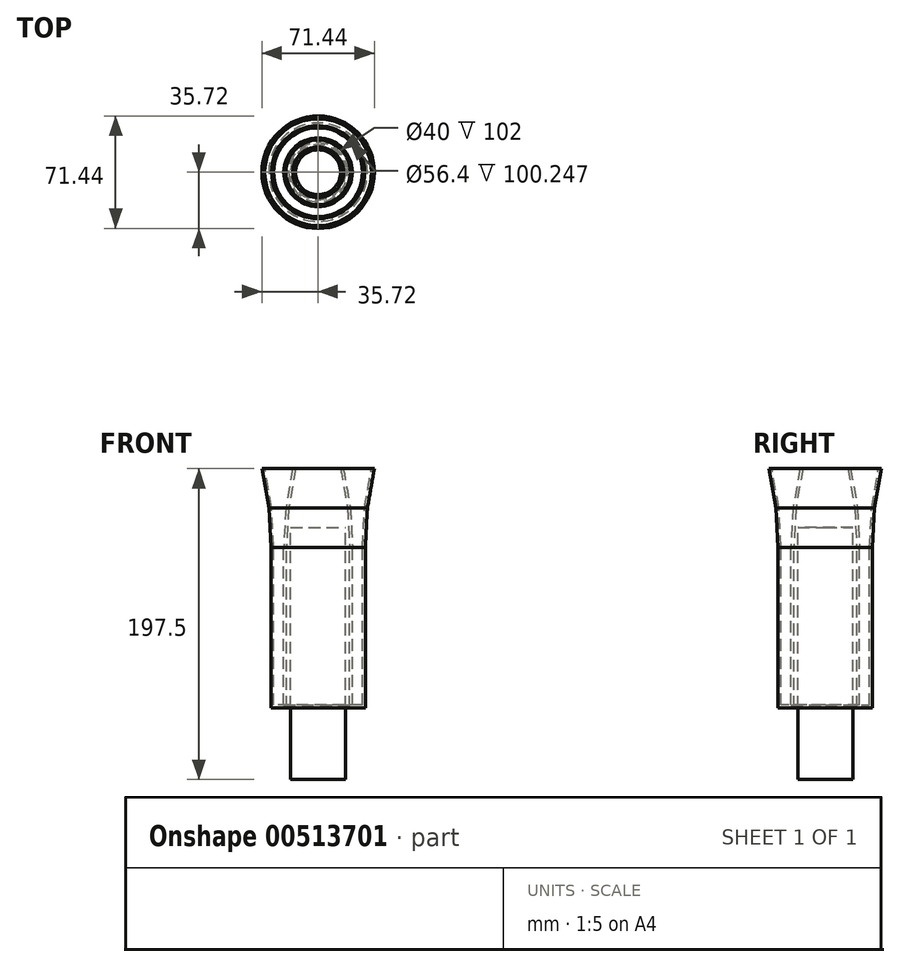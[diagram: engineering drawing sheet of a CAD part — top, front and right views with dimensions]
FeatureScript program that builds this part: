
annotation { "Feature Type Name" : "Feature", "Feature Type Description" : "" }
export const myFeature = defineFeature(function(context is Context, id is Id, definition is map)
    precondition{}
    {
        {
            var Q0;
            Q0=qCreatedBy(makeId("Top.planeOp"),FACE);
            var sketch = newSketch(context, id + "F0", { "sketchPlane" : qUnion([Q0])});
            skCircle(sketch, "E0", {"center": v(0, 0) * mm, "radius": 30 * mm});
            skCircle(sketch, "E1", {"center": v(0, 0) * mm, "radius": 20 * mm});
            skSolve(sketch);
        }
        {
            var Q0;
            Q0=makeQuery(id+"F0.imprint","IMPRINT",FACE,{"disambiguationData":[TD([[makeQuery(id+"F0.imprint","IMPRINT",EDGE,{"derivedFrom":sQuery(id+"F0.wireOp",EDGE,"E0")}),1.0]])]});
            extrude(context, id + "F1", {"entities" : qUnion([Q0]), "depth" : 25 * mm, "hasDraft" : true, "draftAngle" : 3 * degree});
        }
        {
            var Q0;
            Q0=makeQuery(id+"F1.opExtrude","CAP_FACE",FACE,{"disambiguationData":[OSD([sQuery(id+"F0.wireOp",EDGE,"E0"),sQuery(id+"F0.wireOp",EDGE,"E1")])],"isStart":false});
            extrude(context, id + "F2", {"entities" : qUnion([Q0]), "operationType" : NewBodyOperationType.ADD, "depth" : 25 * mm, "hasDraft" : true, "draftAngle" : 10 * degree});
        }
        {
            var Q0;
            Q0=makeQuery(id+"F1.opExtrude","CAP_FACE",FACE,{"disambiguationData":[OSD([sQuery(id+"F0.wireOp",EDGE,"E0"),sQuery(id+"F0.wireOp",EDGE,"E1")])],"isStart":true});
            var sketch = newSketch(context, id + "F3", { "sketchPlane" : qUnion([Q0])});
            skCircle(sketch, "E2", {"center": v(0, 0) * mm, "radius": 17.5 * mm});
            skSolve(sketch);
        }
        {
            var Q0;
            Q0=makeQuery(id+"F3.imprint","IMPRINT",FACE,{"disambiguationData":[TD([[makeQuery(id+"F3.imprint","IMPRINT",EDGE,{"derivedFrom":makeQuery(id+"F1.opExtrude","CAP_EDGE",EDGE,{"disambiguationData":[OSD([sQuery(id+"F0.wireOp",EDGE,"E0")])],"isStart":true})}),-1.0]])]});
            extrude(context, id + "F4", {"entities" : qUnion([Q0]), "operationType" : NewBodyOperationType.ADD, "depth" : 102 * mm, "offsetDistance" : 25 * mm});
        }
        {
            var Q0;
            Q0=makeQuery(id+"F2.opExtrude","CAP_FACE",FACE,{"disambiguationData":[OSD([sQuery(id+"F0.wireOp",EDGE,"E0"),sQuery(id+"F0.wireOp",EDGE,"E1")])],"isStart":false});
            shell(context, id + "F5", {"entities" : qUnion([Q0]), "thickness" : 1.8 * mm});
        }
        {
            var Q0;
            Q0=makeQuery(id+"F3.imprint","IMPRINT",FACE,{"disambiguationData":[TD([[makeQuery(id+"F3.imprint","IMPRINT",EDGE,{"derivedFrom":sQuery(id+"F3.wireOp",EDGE,"E2")}),1.0]])]});
            extrude(context, id + "F6", {"entities" : qUnion([Q0]), "endBound" : BoundingType.SYMMETRIC, "depth" : 25 * mm, "offsetDistance" : 25 * mm});
        }
        {
            var Q0;
            Q0=makeQuery(id+"F6.opExtrude","CAP_FACE",FACE,{"disambiguationData":[OSD([sQuery(id+"F3.wireOp",EDGE,"E2")])],"isStart":false});
            extrude(context, id + "F7", {"entities" : qUnion([Q0]), "operationType" : NewBodyOperationType.ADD, "depth" : 135 * mm, "offsetDistance" : 25 * mm});
        }
    });
